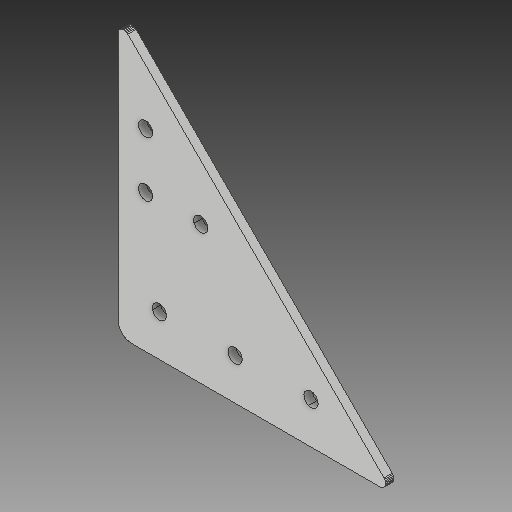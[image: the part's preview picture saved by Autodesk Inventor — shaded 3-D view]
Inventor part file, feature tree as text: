
AUTODESK INVENTOR PART (.ipt)
format: ipt  version: 2018 (Build 220112000, 112)  size: 231,936 bytes
history: native  units: mm
features: other x3, sketch x2, hole x1, projected_geometry x1
ambient origin geometry x8: Origin, YZ Plane, XZ Plane, XY Plane, X Axis, Y Axis, Z Axis, Center Point
bodies: Solid1 (feature_tree)
feature tree (7):
  other  "Side Brace.ipt"
  hole  "Hole1"  [1 undecoded]
  other  "Solid1::Side Brace.ipt"
  other  "TaggingFeature1"
  sketch  "Sketch1"  dims[d0=10.0mm]
  sketch  "Sketch2"  dims[d1=5.2mm d2=6.0mm d3=4.0mm d4=2.0mm d5=90.0deg d6=8.0mm d7=20.594885mm]
  projected_geometry  "Projected Loop1"
note: 1 required parameter value undecoded (feature->parameter linkage not recoverable at this tier; creation-order binding heuristic only, values carry confidence <= 0.55)
